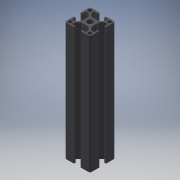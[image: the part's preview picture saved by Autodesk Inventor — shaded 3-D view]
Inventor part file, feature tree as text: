
AUTODESK INVENTOR PART (.ipt)
format: ipt  version: 2016 (Build 200138000, 138)  size: 195,072 bytes
history: native  units: mm
features: other x21, sketch x3, hole x2, extrude x1, pattern_linear x1
ambient origin geometry x8: Origin, YZ Plane, XZ Plane, XY Plane, X Axis, Y Axis, Z Axis, Center Point
bodies: Solid1 (feature_tree)
feature tree (28):
  extrude  "Extrusion1"  Depth=140.0mm
  hole  "Hole1"  [1 undecoded]
  hole  "Hole2"  [1 undecoded]
  pattern_linear  "Rectangular Pattern1"  Spacing1=0.0mm  [1 undecoded]
  other  "C1_XY"
  other  "C1_YZ"
  other  "C1_ZX"
  other  "C1_X"
  other  "C1_Y"
  other  "C1_Z"
  other  "C1_Center"
  other  "to_frame_cap1_XY"
  other  "to_frame_cap1_YZ"
  other  "to_frame_cap1_ZX"
  other  "to_frame_cap1_X"
  other  "to_frame_cap1_Y"
  other  "to_frame_cap1_Z"
  other  "to_frame_cap1_Center"
  other  "to_frame_cap2_XY"
  other  "to_frame_cap2_YZ"
  other  "to_frame_cap2_ZX"
  other  "to_frame_cap2_X"
  other  "to_frame_cap2_Y"
  other  "to_frame_cap2_Z"
  other  "to_frame_cap2_Center"
  sketch  "Sketch_1"  dims[d0=140.0mm d1=0.0mm]
  sketch  "Sketch2"  dims[d2=6.8mm d3=6.0mm d4=4.0mm d5=2.0mm d6=90.0deg d7=140.0mm d8=0.0mm]
  sketch  "Sketch3"  dims[d9=4.2mm d10=6.0mm d11=4.0mm d12=2.0mm d13=90.0deg d14=140.0mm d15=0.0mm d16=20.0mm d18=23.2mm d19=20.0mm d21=23.2mm d22=0.0mm d23=0.0mm d24=0.0mm]
note: 3 required parameter values undecoded (feature->parameter linkage not recoverable at this tier; creation-order binding heuristic only, values carry confidence <= 0.55)
